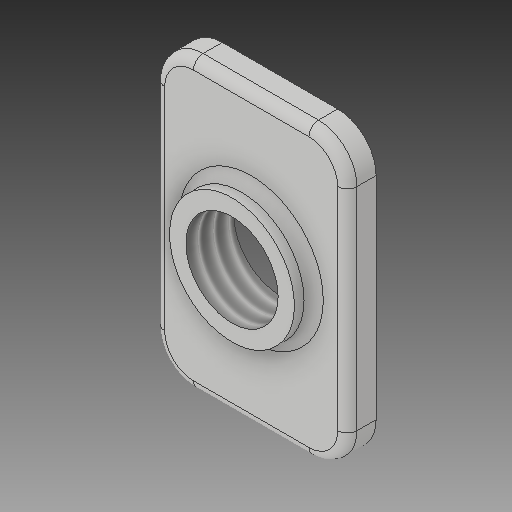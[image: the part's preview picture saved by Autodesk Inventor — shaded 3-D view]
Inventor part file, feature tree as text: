
AUTODESK INVENTOR PART (.ipt)
format: ipt  version: 2018 (Build 220112000, 112)  size: 177,664 bytes
history: native  units: mm
features: other x3, sketch x2
ambient origin geometry x8: Origin, YZ Plane, XZ Plane, XY Plane, X Axis, Y Axis, Z Axis, Center Point
bodies: Solid1 (feature_tree)
feature tree (5):
  other  "M5 Tee Nut-Generic_MIR_CPY.ipt"
  other  "Solid1::M5 Tee Nut-Generic_MIR_CPY.ipt"
  other  "TaggingFeature1"
  sketch  "Sketch1"  dims[d0=10.0mm]
  sketch  "Sketch2"
